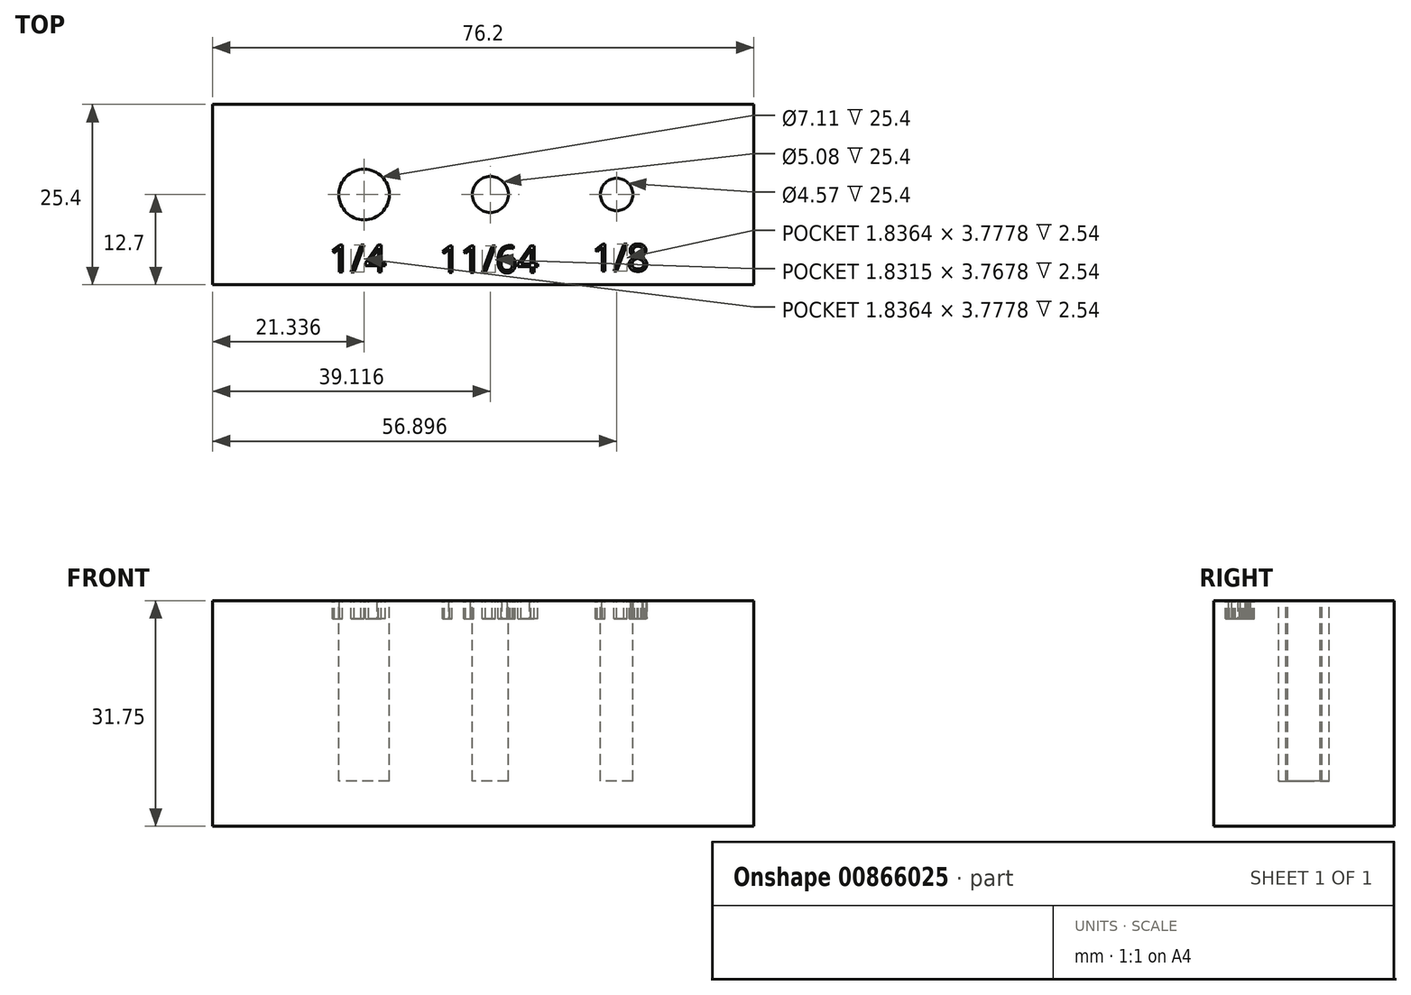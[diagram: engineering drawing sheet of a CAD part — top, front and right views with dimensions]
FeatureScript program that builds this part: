
annotation { "Feature Type Name" : "Feature", "Feature Type Description" : "" }
export const myFeature = defineFeature(function(context is Context, id is Id, definition is map)
    precondition{}
    {
        {
            var Q0;
            Q0=qCreatedBy(makeId("Top.planeOp"),FACE);
            var sketch = newSketch(context, id + "F0", { "sketchPlane" : qUnion([Q0])});
            skLineSegment(sketch, "E0.bottom", {"start": v(38.1, -12.7) * mm, "end": v(-38.1, -12.7) * mm});
            skLineSegment(sketch, "E0.top", {"start": v(38.1, 12.7) * mm, "end": v(-38.1, 12.7) * mm});
            skLineSegment(sketch, "E0.left", {"start": v(38.1, -12.7) * mm, "end": v(38.1, 12.7) * mm});
            skLineSegment(sketch, "E0.right", {"start": v(-38.1, -12.7) * mm, "end": v(-38.1, 12.7) * mm});
            skPoint(sketch, "E0.middle", {"position": v(0, 0) * mm});
            skSolve(sketch);
        }
        {
            var Q0;
            Q0=qSketchRegion(id+"F0",true);
            extrude(context, id + "F1", {"entities" : qUnion([Q0]), "depth" : 31.75 * mm, "offsetDistance" : 25.4 * mm});
        }
        {
            var Q0;
            Q0=makeQuery(id+"F1.opExtrude","CAP_FACE",FACE,{"disambiguationData":[OSD([sQuery(id+"F0.wireOp",EDGE,"E0.bottom"),sQuery(id+"F0.wireOp",EDGE,"E0.top"),sQuery(id+"F0.wireOp",EDGE,"E0.left"),sQuery(id+"F0.wireOp",EDGE,"E0.right")])],"isStart":false});
            var sketch = newSketch(context, id + "F2", { "sketchPlane" : qUnion([Q0])});
            skLineSegment(sketch, "E1", {"start": v(0, 0) * mm, "end": v(96.77, 0) * mm});
            skPoint(sketch, "E1.endSnap0", {"position": v(38.1, 0) * mm});
            skLineSegment(sketch, "E2", {"start": v(0, 0) * mm, "end": v(-135.48, 0) * mm});
            skCircle(sketch, "E3", {"center": v(-16.76, 0) * mm, "radius": 3.56 * mm});
            skCircle(sketch, "E4", {"center": v(1.02, 0) * mm, "radius": 2.54 * mm});
            skCircle(sketch, "E5", {"center": v(18.8, 0) * mm, "radius": 2.29 * mm});
            skSolve(sketch);
        }
        {
            var Q0;
            Q0=qSketchRegion(id+"F2",true);
            extrude(context, id + "F3", {"entities" : qUnion([Q0]), "operationType" : NewBodyOperationType.REMOVE, "oppositeDirection" : true, "depth" : 25.4 * mm, "offsetDistance" : 25.4 * mm});
        }
        {
            var Q0;
            {var subQ0=sQuery(id+"F0.wireOp",EDGE,"E0.left");var subQ1=sQuery(id+"F0.wireOp",EDGE,"E0.right");var subQ2=sQuery(id+"F0.wireOp",EDGE,"E0.bottom");var subQ3=sQuery(id+"F0.wireOp",EDGE,"E0.top");Q0=makeQuery(id+"F3.boolean.opBoolean","SPLIT",FACE,{"disambiguationData":[TD([makeQuery(id+"F1.opExtrude","SWEPT_FACE",FACE,{"disambiguationData":[OSD([subQ2])]})])],"derivedFrom":makeQuery(id+"F1.opExtrude","CAP_FACE",FACE,{"disambiguationData":[OSD([subQ2,subQ3,subQ0,subQ1])],"isStart":false})});}
            var sketch = newSketch(context, id + "F4", { "sketchPlane" : qUnion([Q0])});
            skText(sketch, "E6", { "text": "1/4", "fontName": "OpenSans-Regular.ttf"});
            skText(sketch, "E7", { "text": "11/64\n", "fontName": "OpenSans-Regular.ttf"});
            skText(sketch, "E8", { "text": "1/8\n", "fontName": "OpenSans-Regular.ttf"});
            const initialGuessF4  = {"E6": [-0.02167, -0.0109, 1, 0, 0.00381], "E7": [-0.0062, -0.011, 1, 0, 0.0038], "E8": [0.01532, -0.01078, 1, 0, 0.00381]};
            skSetInitialGuess(sketch, initialGuessF4);
            skSolve(sketch);
        }
        {
            var Q0;
            Q0 = qSketchRegion(id + "F4", true);
            extrude(context, id + "F5", {"entities" : qUnion([Q0]), "operationType" : NewBodyOperationType.REMOVE, "oppositeDirection" : true, "depth" : 2.54 * mm, "offsetDistance" : 25.4 * mm});
        }
    });
